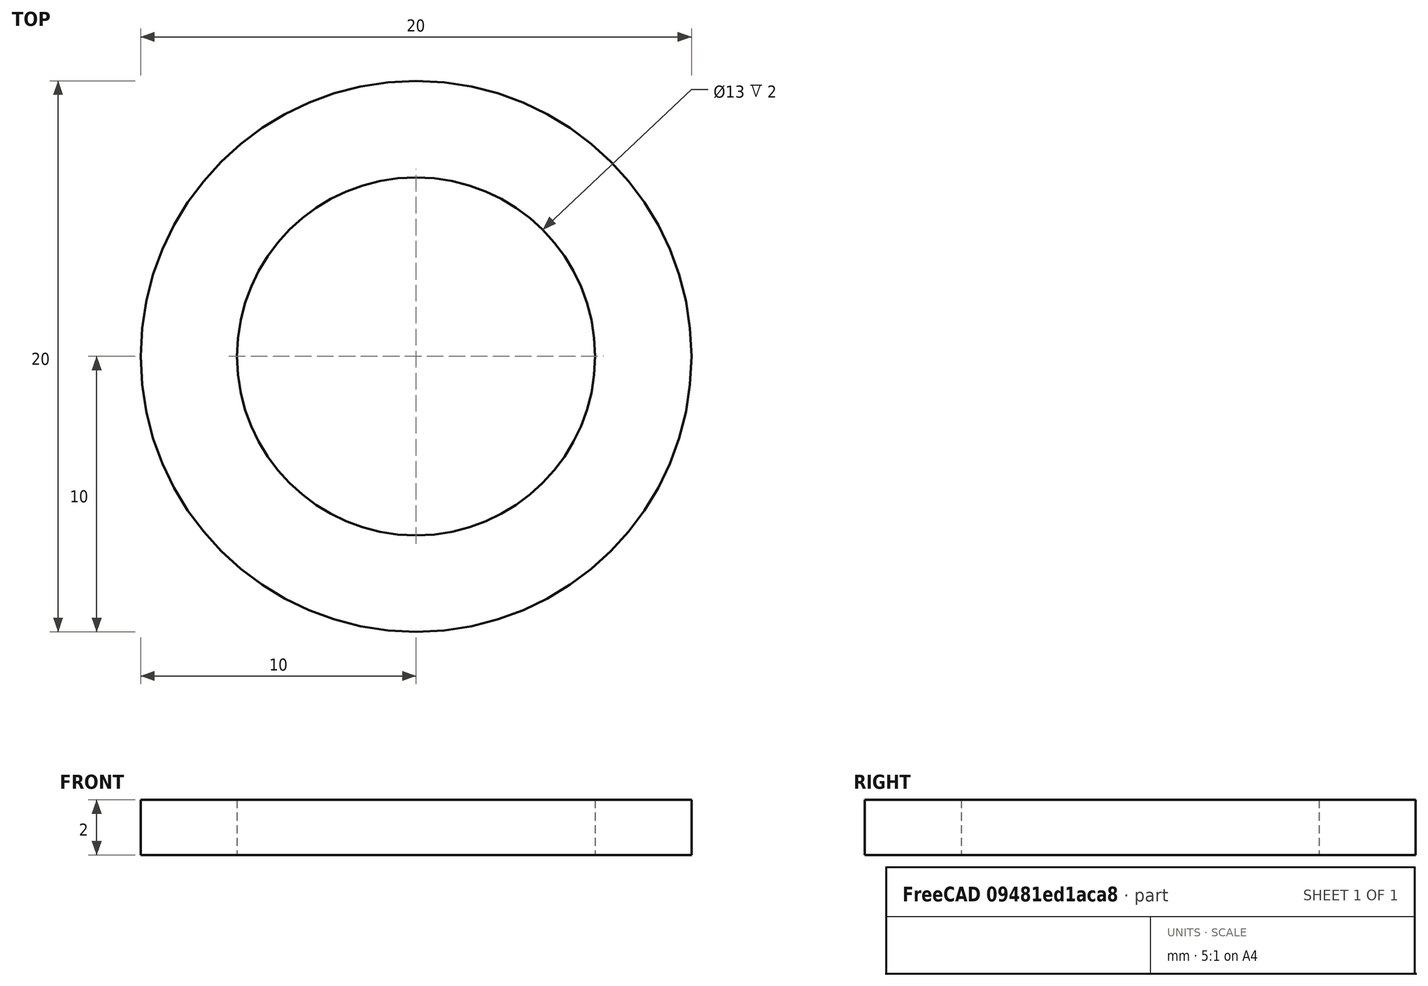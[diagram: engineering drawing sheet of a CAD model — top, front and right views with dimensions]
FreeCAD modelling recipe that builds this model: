
FCSTD DOCUMENT  (FreeCAD 0.14R3700 (Git))
Label: Scheibe DIN 433 - A 13
License: CC-BY 3.0
LicenseURL: http://creativecommons.org/licenses/by/3.0/
objects: Sketcher::SketchObject×1, PartDesign::Revolution×1, Part::Feature×1
note: 4 computed .brp shape members not serialized (recipe doc carries the construction recipe); baked Part::Feature solids carry a one-line shape summary decoded from their .brp

FEATURE [Sketcher::SketchObject] Sketch
  Placement = pos=(0,0,0) rot=(0.57735,0.57735,0.57735;2.0944rad)
  sketch-geometry (4):
    g0: LineSegment StartX=6.5 StartY=0 StartZ=0 EndX=10 EndY=0 EndZ=0
    g1: LineSegment StartX=10 StartY=0 StartZ=0 EndX=10 EndY=2 EndZ=0
    g2: LineSegment StartX=10 StartY=2 StartZ=0 EndX=6.5 EndY=2 EndZ=0
    g3: LineSegment StartX=6.5 StartY=2 StartZ=0 EndX=6.5 EndY=0 EndZ=0
  constraints (12):
    c: Coincident(g0,g1)
    c: Coincident(g1,g2)
    c: Coincident(g2,g3)
    c: Coincident(g3,g0)
    c: Horizontal(g0)
    c: Horizontal(g2)
    c: Vertical(g1)
    c: Vertical(g3)
    c: PointOnObject(g0,g-1)
    c: DistanceY(g1) = 2
    c: DistanceX(g-1,g2) = 6.5
    c: DistanceX(g-1,g1) = 10
FEATURE [PartDesign::Revolution] Revolution  label="Scheibe DIN 433 - A 13 #"
  Angle = 360
  Axis = (0,0,1)
  Base = (0,0,0)
  Placement = pos=(0,0,0) rot=(0.57735,0.57735,0.57735;2.0944rad)
  ReferenceAxis = -> Sketch [V_Axis]
  Reversed = true
  Sketch = -> Sketch
FEATURE [Part::Feature] Revolution001  label="Scheibe DIN 433 - A 13 #001"
  Placement = pos=(0,0,0) rot=(0.57735,0.57735,0.57735;2.0944rad)
  shape: bbox 20 x 20 x 2 mm, 4 faces (baked)
